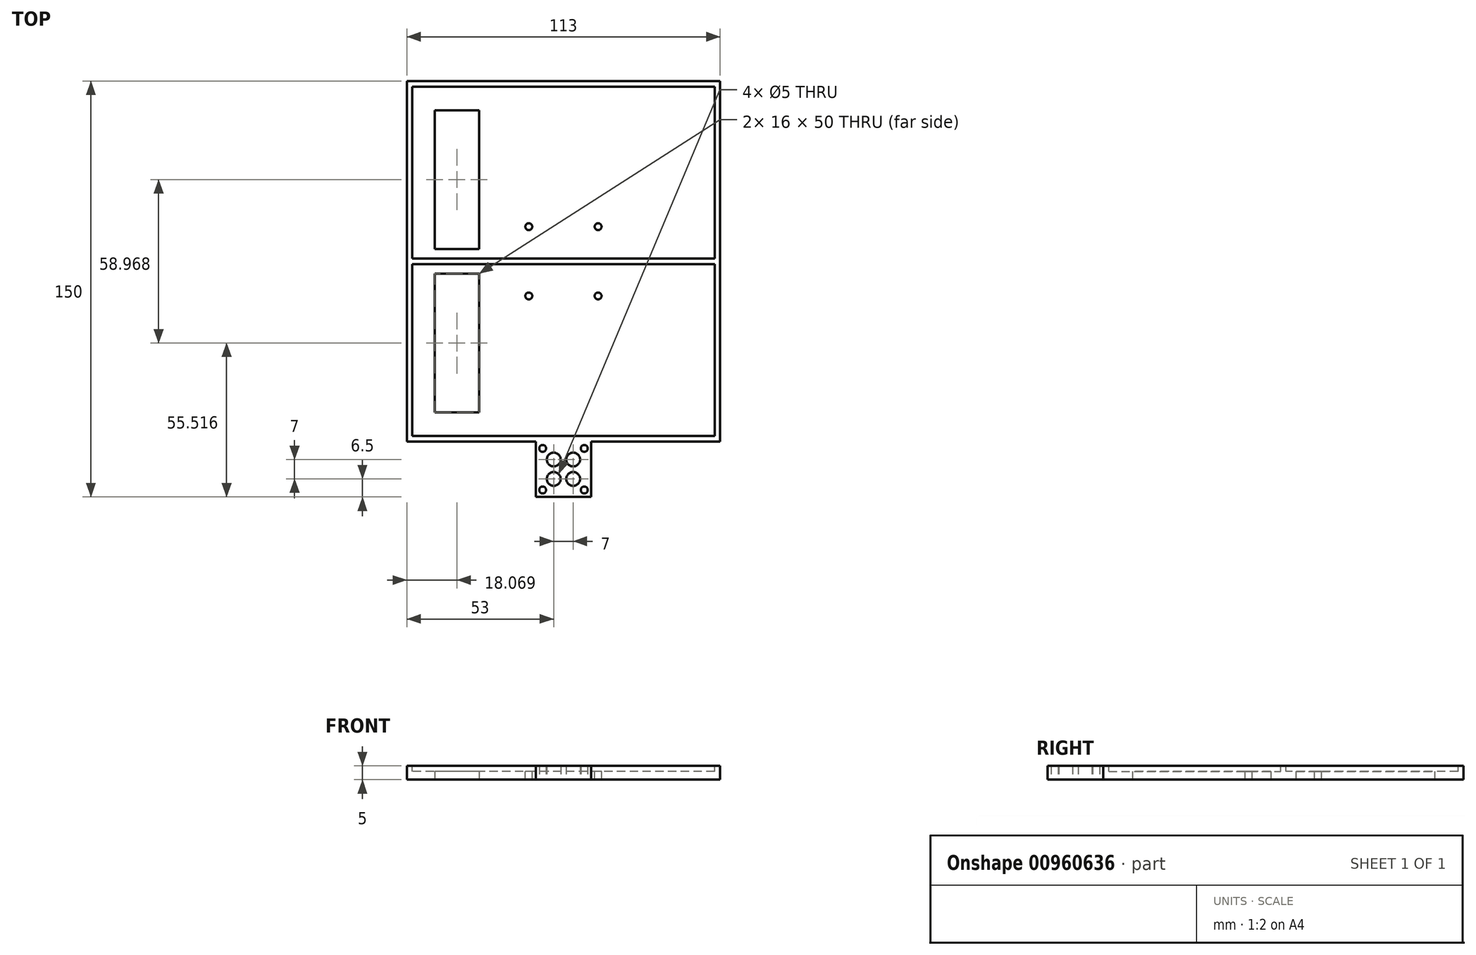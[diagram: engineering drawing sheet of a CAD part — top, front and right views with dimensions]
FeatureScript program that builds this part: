
annotation { "Feature Type Name" : "Feature", "Feature Type Description" : "" }
export const myFeature = defineFeature(function(context is Context, id is Id, definition is map)
    precondition{}
    {
        {
            var Q0;
            Q0=qCreatedBy(makeId("Top.planeOp"),FACE);
            var sketch = newSketch(context, id + "F0", { "sketchPlane" : qUnion([Q0])});
            skLineSegment(sketch, "E0.bottom", {"start": v(56.5, 65) * mm, "end": v(-56.5, 65) * mm});
            skLineSegment(sketch, "E0.top", {"start": v(56.5, -65) * mm, "end": v(-56.5, -65) * mm});
            skLineSegment(sketch, "E0.left", {"start": v(56.5, 65) * mm, "end": v(56.5, -65) * mm});
            skLineSegment(sketch, "E0.right", {"start": v(-56.5, 65) * mm, "end": v(-56.5, -65) * mm});
            skPoint(sketch, "E0.middle", {"position": v(0, 0) * mm});
            skLineSegment(sketch, "E1.bottom", {"start": v(10, -45) * mm, "end": v(-10, -45) * mm});
            skLineSegment(sketch, "E1.top", {"start": v(10, -85) * mm, "end": v(-10, -85) * mm});
            skLineSegment(sketch, "E1.left", {"start": v(10, -45) * mm, "end": v(10, -85) * mm});
            skLineSegment(sketch, "E1.right", {"start": v(-10, -45) * mm, "end": v(-10, -85) * mm});
            skPoint(sketch, "E1.middle", {"position": v(0, -65) * mm});
            skSolve(sketch);
        }
        {
            var Q0;
            Q0 = qSketchRegion(id + "F0", true);
            extrude(context, id + "F1", {"entities" : qUnion([Q0]), "depth" : 5 * mm, "offsetDistance" : 25 * mm});
        }
        {
            var Q0;
            Q0=makeQuery(id+"F1.opExtrude","CAP_FACE",FACE,{"disambiguationData":[OSD([sQuery(id+"F0.wireOp",EDGE,"E0.bottom"),sQuery(id+"F0.wireOp",EDGE,"E0.top"),sQuery(id+"F0.wireOp",EDGE,"E0.left"),sQuery(id+"F0.wireOp",EDGE,"E0.right"),sQuery(id+"F0.wireOp",EDGE,"E1.top"),sQuery(id+"F0.wireOp",EDGE,"E1.left"),sQuery(id+"F0.wireOp",EDGE,"E1.right")])],"isStart":false});
            var sketch = newSketch(context, id + "F2", { "sketchPlane" : qUnion([Q0])});
            skPoint(sketch, "E2", {"position": v(-7.5, -82.5) * mm});
            skLineSegment(sketch, "E3", {"start": v(0, -85) * mm, "end": v(0, -57.9) * mm, "construction": true});
            skLineSegment(sketch, "E4", {"start": v(-10, -75) * mm, "end": v(10, -75) * mm, "construction": true});
            skPoint(sketch, "E5", {"position": v(-3.5, -78.5) * mm});
            skPoint(sketch, "E6.MirrorP", {"position": v(-3.5, -71.5) * mm});
            skPoint(sketch, "E7.MirrorP", {"position": v(-7.5, -67.5) * mm});
            skPoint(sketch, "E8.MirrorP", {"position": v(3.5, -78.5) * mm});
            skPoint(sketch, "E9.MirrorP", {"position": v(7.5, -82.5) * mm});
            skPoint(sketch, "E10.MirrorP", {"position": v(3.5, -71.5) * mm});
            skPoint(sketch, "E11.MirrorP", {"position": v(7.5, -67.5) * mm});
            skSolve(sketch);
        }
        {
            var Q0;
            Q0=sQuery(id+"F2.wireOp",VERTEX,"E2");
            var Q1;
            Q1=sQuery(id+"F2.wireOp",VERTEX,"E7.MirrorP");
            var Q2;
            Q2=sQuery(id+"F2.wireOp",VERTEX,"E11.MirrorP");
            var Q3;
            Q3=sQuery(id+"F2.wireOp",VERTEX,"E9.MirrorP");
            var Q4;
            Q4=makeQuery(id+"F1.opExtrude","SWEPT_BODY",BODY,{"disambiguationData":[OSD([sQuery(id+"F0.wireOp",EDGE,"E0.bottom"),sQuery(id+"F0.wireOp",EDGE,"E0.top"),sQuery(id+"F0.wireOp",EDGE,"E0.left"),sQuery(id+"F0.wireOp",EDGE,"E0.right"),sQuery(id+"F0.wireOp",EDGE,"E1.top"),sQuery(id+"F0.wireOp",EDGE,"E1.left"),sQuery(id+"F0.wireOp",EDGE,"E1.right")])]});
            hole(context, id + "F3", {"style" : HoleStyle.SIMPLE, "endStyle" : HoleEndStyle.THROUGH, "standardTappedOrClearance" : lookupTablePath({ "standard" : "ISO", "engagement" : "75%", "pitch" : "0.5 mm", "size" : "M3", "type" : "Tapped" }), "standardBlindInLast" : lookupTablePath({ "standard" : "ISO", "fit" : "Normal", "engagement" : "75%", "pitch" : "0.5 mm", "size" : "M3", "type" : "Clearance & tapped" }), "holeDiameter" : 2.5 * mm, "majorDiameter" : 3 * mm, "showTappedDepth" : true, "isTappedThrough" : true, "tappedDepth" : 18.5 * mm, "tapClearance" : 3, "locations" : qUnion([Q0, Q1, Q2, Q3]), "scope" : qUnion([Q4]), "startStyle" : HoleStartStyle.PART});
        }
        {
            var Q0;
            Q0=sQuery(id+"F2.wireOp",VERTEX,"E6.MirrorP");
            var Q1;
            Q1=sQuery(id+"F2.wireOp",VERTEX,"E10.MirrorP");
            var Q2;
            Q2=sQuery(id+"F2.wireOp",VERTEX,"E8.MirrorP");
            var Q3;
            Q3=sQuery(id+"F2.wireOp",VERTEX,"E5");
            var Q4;
            Q4=makeQuery(id+"F1.opExtrude","SWEPT_BODY",BODY,{"disambiguationData":[OSD([sQuery(id+"F0.wireOp",EDGE,"E0.bottom"),sQuery(id+"F0.wireOp",EDGE,"E0.top"),sQuery(id+"F0.wireOp",EDGE,"E0.left"),sQuery(id+"F0.wireOp",EDGE,"E0.right"),sQuery(id+"F0.wireOp",EDGE,"E1.top"),sQuery(id+"F0.wireOp",EDGE,"E1.left"),sQuery(id+"F0.wireOp",EDGE,"E1.right")])]});
            hole(context, id + "F4", {"style" : HoleStyle.SIMPLE, "endStyle" : HoleEndStyle.THROUGH, "holeDiameter" : 5 * mm, "majorDiameter" : 3 * mm, "isTappedThrough" : true, "tappedDepth" : 18.5 * mm, "tapClearance" : 3, "locations" : qUnion([Q0, Q1, Q2, Q3]), "scope" : qUnion([Q4]), "startStyle" : HoleStartStyle.PART});
        }
        {
            var Q0;
            Q0=makeQuery(id+"F1.opExtrude","CAP_FACE",FACE,{"disambiguationData":[OSD([sQuery(id+"F0.wireOp",EDGE,"E0.bottom"),sQuery(id+"F0.wireOp",EDGE,"E0.top"),sQuery(id+"F0.wireOp",EDGE,"E0.left"),sQuery(id+"F0.wireOp",EDGE,"E0.right"),sQuery(id+"F0.wireOp",EDGE,"E1.top"),sQuery(id+"F0.wireOp",EDGE,"E1.left"),sQuery(id+"F0.wireOp",EDGE,"E1.right")])],"isStart":false});
            var sketch = newSketch(context, id + "F5", { "sketchPlane" : qUnion([Q0])});
            skLineSegment(sketch, "E12", {"start": v(-56.5, 0) * mm, "end": v(56.5, 0) * mm, "construction": true});
            skPoint(sketch, "E13", {"position": v(0, 32) * mm});
            skLineSegment(sketch, "E14.bottom", {"start": v(54.5, 63) * mm, "end": v(-54.5, 63) * mm});
            skLineSegment(sketch, "E14.top", {"start": v(54.5, 1) * mm, "end": v(-54.5, 1) * mm});
            skLineSegment(sketch, "E14.left", {"start": v(54.5, 63) * mm, "end": v(54.5, 1) * mm});
            skLineSegment(sketch, "E14.right", {"start": v(-54.5, 63) * mm, "end": v(-54.5, 1) * mm});
            skLineSegment(sketch, "E15.MirrorCS", {"start": v(54.5, -1) * mm, "end": v(-54.5, -1) * mm});
            skLineSegment(sketch, "E16.MirrorCS", {"start": v(-54.5, -63) * mm, "end": v(-54.5, -1) * mm});
            skLineSegment(sketch, "E17.MirrorCS", {"start": v(54.5, -63) * mm, "end": v(-54.5, -63) * mm});
            skLineSegment(sketch, "E18.MirrorCS", {"start": v(54.5, -63) * mm, "end": v(54.5, -1) * mm});
            skSolve(sketch);
        }
        {
            var Q0;
            Q0 = qSketchRegion(id + "F5", true);
            extrude(context, id + "F6", {"entities" : qUnion([Q0]), "operationType" : NewBodyOperationType.REMOVE, "oppositeDirection" : true, "depth" : 2 * mm, "offsetDistance" : 25 * mm});
        }
        {
            var Q0;
            Q0=makeQuery(id+"F1.opExtrude","CAP_FACE",FACE,{"disambiguationData":[OSD([sQuery(id+"F0.wireOp",EDGE,"E0.bottom"),sQuery(id+"F0.wireOp",EDGE,"E0.top"),sQuery(id+"F0.wireOp",EDGE,"E0.left"),sQuery(id+"F0.wireOp",EDGE,"E0.right"),sQuery(id+"F0.wireOp",EDGE,"E1.top"),sQuery(id+"F0.wireOp",EDGE,"E1.left"),sQuery(id+"F0.wireOp",EDGE,"E1.right")])],"isStart":true});
            var sketch = newSketch(context, id + "F7", { "sketchPlane" : qUnion([Q0])});
            skLineSegment(sketch, "E19.bottom", {"start": v(15, 15) * mm, "end": v(-15, 15) * mm, "construction": true});
            skLineSegment(sketch, "E19.top", {"start": v(15, -15) * mm, "end": v(-15, -15) * mm, "construction": true});
            skLineSegment(sketch, "E19.left", {"start": v(15, 15) * mm, "end": v(15, -15) * mm, "construction": true});
            skLineSegment(sketch, "E19.right", {"start": v(-15, 15) * mm, "end": v(-15, -15) * mm, "construction": true});
            skPoint(sketch, "E19.middle", {"position": v(0, 0) * mm});
            skPoint(sketch, "E20", {"position": v(-12.5, 12.5) * mm});
            skLineSegment(sketch, "E21", {"start": v(0, 85) * mm, "end": v(0, -65) * mm, "construction": true});
            skLineSegment(sketch, "E22", {"start": v(-56.5, 0) * mm, "end": v(56.5, 0) * mm, "construction": true});
            skPoint(sketch, "E23.MirrorP", {"position": v(12.5, 12.5) * mm});
            skPoint(sketch, "E24.MirrorP", {"position": v(-12.5, -12.5) * mm});
            skPoint(sketch, "E25.MirrorP", {"position": v(12.5, -12.5) * mm});
            skSolve(sketch);
        }
        {
            var Q0;
            Q0=sQuery(id+"F7.wireOp",VERTEX,"E20");
            var Q1;
            Q1=sQuery(id+"F7.wireOp",VERTEX,"E23.MirrorP");
            var Q2;
            Q2=sQuery(id+"F7.wireOp",VERTEX,"E25.MirrorP");
            var Q3;
            Q3=sQuery(id+"F7.wireOp",VERTEX,"E24.MirrorP");
            var Q4;
            Q4=makeQuery(id+"F1.opExtrude","SWEPT_BODY",BODY,{"disambiguationData":[OSD([sQuery(id+"F0.wireOp",EDGE,"E0.bottom"),sQuery(id+"F0.wireOp",EDGE,"E0.top"),sQuery(id+"F0.wireOp",EDGE,"E0.left"),sQuery(id+"F0.wireOp",EDGE,"E0.right"),sQuery(id+"F0.wireOp",EDGE,"E1.top"),sQuery(id+"F0.wireOp",EDGE,"E1.left"),sQuery(id+"F0.wireOp",EDGE,"E1.right")])]});
            hole(context, id + "F8", {"style" : HoleStyle.SIMPLE, "endStyle" : HoleEndStyle.THROUGH, "standardTappedOrClearance" : lookupTablePath({ "standard" : "ISO", "engagement" : "75%", "pitch" : "0.5 mm", "size" : "M3", "type" : "Tapped" }), "standardBlindInLast" : lookupTablePath({ "standard" : "ISO", "fit" : "Normal", "engagement" : "75%", "pitch" : "0.5 mm", "size" : "M3", "type" : "Clearance & tapped" }), "holeDiameter" : 2.5 * mm, "majorDiameter" : 3 * mm, "showTappedDepth" : true, "isTappedThrough" : true, "tappedDepth" : 0.5 * mm, "tapClearance" : 3, "locations" : qUnion([Q0, Q1, Q2, Q3]), "scope" : qUnion([Q4]), "startStyle" : HoleStartStyle.PART});
        }
        {
            var Q0;
            Q0=makeQuery(id+"F1.opExtrude","CAP_FACE",FACE,{"disambiguationData":[OSD([sQuery(id+"F0.wireOp",EDGE,"E0.bottom"),sQuery(id+"F0.wireOp",EDGE,"E0.top"),sQuery(id+"F0.wireOp",EDGE,"E0.left"),sQuery(id+"F0.wireOp",EDGE,"E0.right"),sQuery(id+"F0.wireOp",EDGE,"E1.top"),sQuery(id+"F0.wireOp",EDGE,"E1.left"),sQuery(id+"F0.wireOp",EDGE,"E1.right")])],"isStart":true});
            var sketch = newSketch(context, id + "F9", { "sketchPlane" : qUnion([Q0])});
            skLineSegment(sketch, "E26", {"start": v(0, -65) * mm, "end": v(0, 63.78) * mm, "construction": true});
            skPoint(sketch, "E27", {"position": v(-37.55, 0) * mm});
            skLineSegment(sketch, "E28", {"start": v(-56.5, 0) * mm, "end": v(56.5, 0) * mm, "construction": true});
            skLineSegment(sketch, "E29.bottom", {"start": v(-46.43, 54.48) * mm, "end": v(-30.43, 54.48) * mm});
            skLineSegment(sketch, "E29.top", {"start": v(-46.43, 4.48) * mm, "end": v(-30.43, 4.48) * mm});
            skLineSegment(sketch, "E29.left", {"start": v(-46.43, 54.48) * mm, "end": v(-46.43, 4.48) * mm});
            skLineSegment(sketch, "E29.right", {"start": v(-30.43, 54.48) * mm, "end": v(-30.43, 4.48) * mm});
            skLineSegment(sketch, "E30.MirrorCS", {"start": v(-30.43, -54.48) * mm, "end": v(-30.43, -4.48) * mm});
            skLineSegment(sketch, "E31.MirrorCS", {"start": v(-46.43, -4.48) * mm, "end": v(-30.43, -4.48) * mm});
            skLineSegment(sketch, "E32.MirrorCS", {"start": v(-46.43, -54.48) * mm, "end": v(-46.43, -4.48) * mm});
            skLineSegment(sketch, "E33.MirrorCS", {"start": v(-46.43, -54.48) * mm, "end": v(-30.43, -54.48) * mm});
            skSolve(sketch);
        }
        {
            var Q0;
            Q0=makeQuery(id+"F9.imprint","IMPRINT",FACE,{"disambiguationData":[TD([[makeQuery(id+"F9.imprint","IMPRINT",EDGE,{"derivedFrom":sQuery(id+"F9.wireOp",EDGE,"E29.bottom")}),-1.0]])]});
            var Q1;
            Q1=makeQuery(id+"F9.imprint","IMPRINT",FACE,{"disambiguationData":[TD([[makeQuery(id+"F9.imprint","IMPRINT",EDGE,{"derivedFrom":sQuery(id+"F9.wireOp",EDGE,"E30.MirrorCS")}),1.0]])]});
            extrude(context, id + "F10", {"entities" : qUnion([Q0, Q1]), "operationType" : NewBodyOperationType.REMOVE, "endBound" : BoundingType.THROUGH_ALL, "oppositeDirection" : true, "depth" : 25 * mm, "offsetDistance" : 25 * mm});
        }
    });
